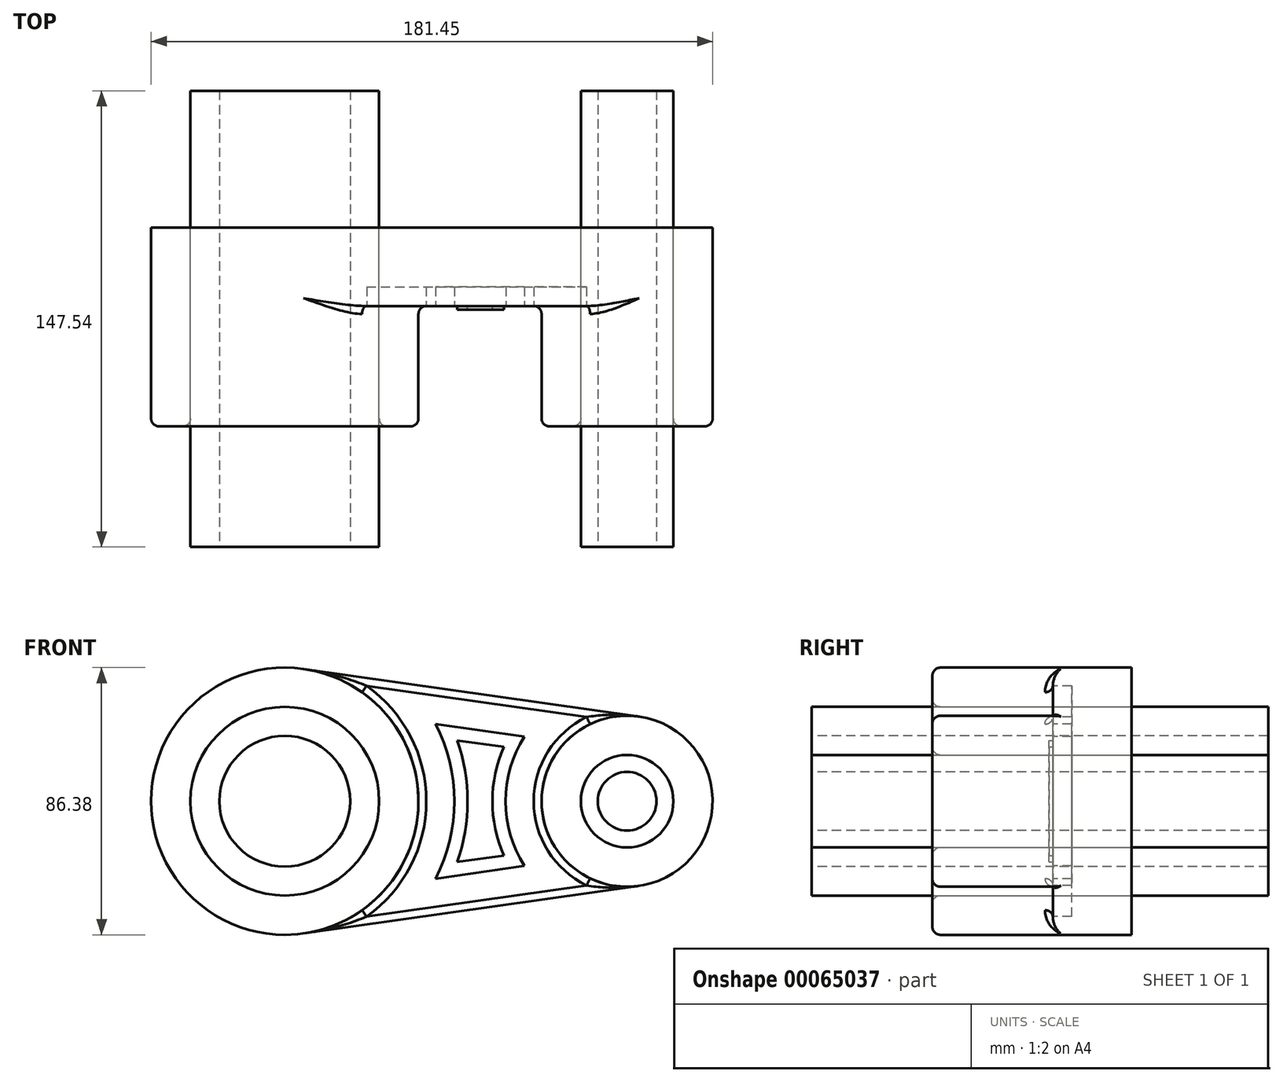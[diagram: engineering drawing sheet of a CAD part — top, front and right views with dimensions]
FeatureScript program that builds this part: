
annotation { "Feature Type Name" : "Feature", "Feature Type Description" : "" }
export const myFeature = defineFeature(function(context is Context, id is Id, definition is map)
    precondition{}
    {
        {
            var Q0;
            Q0=qCreatedBy(makeId("Front.planeOp"),FACE);
            var sketch = newSketch(context, id + "F0", { "sketchPlane" : qUnion([Q0])});
            skCircle(sketch, "E0", {"center": v(-144.17, 0) * mm, "radius": 43.2 * mm});
            skCircle(sketch, "E1", {"center": v(-33.55, 0) * mm, "radius": 27.65 * mm});
            skLineSegment(sketch, "E2", {"start": v(-138.1, -42.76) * mm, "end": v(-29.67, -27.37) * mm});
            skLineSegment(sketch, "E3", {"start": v(-138.1, 42.76) * mm, "end": v(-29.67, 27.37) * mm});
            skCircle(sketch, "E4.0", {"center": v(-144.17, 0) * mm, "radius": 30.5 * mm});
            skCircle(sketch, "E5.0", {"center": v(-33.55, 0) * mm, "radius": 14.95 * mm});
            skSolve(sketch);
        }
        {
            var Q0;
            Q0=makeQuery(id+"F0.imprint","IMPRINT",FACE,{"disambiguationData":[TD([[makeQuery(id+"F0.imprint","IMPRINT",EDGE,{"derivedFrom":sQuery(id+"F0.wireOp",EDGE,"E5.0")}),-1.0]])]});
            var Q1;
            {var subQ0=sQuery(id+"F0.wireOp",EDGE,"E2");Q1=makeQuery(id+"F0.imprint","IMPRINT",FACE,{"disambiguationData":[TD([[makeQuery(id+"F0.imprint","IMPRINT",EDGE,{"derivedFrom":subQ0}),1.0]])]});}
            var Q2;
            Q2=makeQuery(id+"F0.imprint","IMPRINT",FACE,{"disambiguationData":[TD([[makeQuery(id+"F0.imprint","IMPRINT",EDGE,{"derivedFrom":sQuery(id+"F0.wireOp",EDGE,"E4.0")}),-1.0]])]});
            extrude(context, id + "F1", {"entities" : qUnion([Q0, Q1, Q2]), "depth" : 25.4 * mm});
        }
        {
            var Q0;
            Q0=makeQuery(id+"F0.imprint","IMPRINT",FACE,{"disambiguationData":[TD([[makeQuery(id+"F0.imprint","IMPRINT",EDGE,{"derivedFrom":sQuery(id+"F0.wireOp",EDGE,"E4.0")}),-1.0]])]});
            var Q1;
            Q1=makeQuery(id+"F0.imprint","IMPRINT",FACE,{"disambiguationData":[TD([[makeQuery(id+"F0.imprint","IMPRINT",EDGE,{"derivedFrom":sQuery(id+"F0.wireOp",EDGE,"E5.0")}),-1.0]])]});
            extrude(context, id + "F2", {"entities" : qUnion([Q0, Q1]), "operationType" : NewBodyOperationType.ADD, "depth" : 64.3 * mm});
        }
        {
            var Q0;
            Q0=makeQuery(id+"F2.opExtrude","CAP_FACE",FACE,{"disambiguationData":[OSD([sQuery(id+"F0.wireOp",EDGE,"E0"),sQuery(id+"F0.wireOp",EDGE,"E4.0")])],"isStart":false});
            var Q1;
            Q1=makeQuery(id+"F2.opExtrude","CAP_FACE",FACE,{"disambiguationData":[OSD([sQuery(id+"F0.wireOp",EDGE,"E1"),sQuery(id+"F0.wireOp",EDGE,"E5.0")])],"isStart":false});
            var Q2;
            Q2=makeQuery(id+"F1.opExtrude","CAP_FACE",FACE,{"disambiguationData":[OSD([sQuery(id+"F0.wireOp",EDGE,"E0"),sQuery(id+"F0.wireOp",EDGE,"E1"),sQuery(id+"F0.wireOp",EDGE,"E2"),sQuery(id+"F0.wireOp",EDGE,"E3"),sQuery(id+"F0.wireOp",EDGE,"E4.0"),sQuery(id+"F0.wireOp",EDGE,"E5.0")])],"isStart":false});
            fillet(context, id + "F3", {"entities" : qUnion([Q0, Q1, Q2]), "radius" : 2.54 * mm, "tangentPropagation" : true, "allowEdgeOverflow" : false});
        }
        {
            var Q0;
            Q0=makeQuery(id+"F2.opExtrude","CAP_FACE",FACE,{"disambiguationData":[OSD([sQuery(id+"F0.wireOp",EDGE,"E0"),sQuery(id+"F0.wireOp",EDGE,"E4.0")])],"isStart":false});
            var sketch = newSketch(context, id + "F4", { "sketchPlane" : qUnion([Q0])});
            skCircle(sketch, "E6.0", {"center": v(-144.17, 0) * mm, "radius": 30.5 * mm});
            skCircle(sketch, "E6.1", {"center": v(-33.55, 0) * mm, "radius": 14.95 * mm});
            skSolve(sketch);
        }
        {
            var Q0;
            Q0 = qSketchRegion(id + "F4", true);
            extrude(context, id + "F5", {"entities" : qUnion([Q0]), "depth" : 147.53 * mm});
        }
        {
            var Q0;
            Q0=makeQuery(id+"F5.opExtrude","SWEPT_BODY",BODY,{"disambiguationData":[OSD([sQuery(id+"F4.wireOp",EDGE,"E6.0")])]});
            var Q1;
            Q1=makeQuery(id+"F5.opExtrude","SWEPT_BODY",BODY,{"disambiguationData":[OSD([sQuery(id+"F4.wireOp",EDGE,"E6.1")])]});
            transform(context, id + "F6", {"entities" : qUnion([Q0, Q1]), "transformType" : TransformType.TRANSLATION_3D, "dx" : 0 * mm, "dy" : 90.18 * mm, "dz" : 0 * mm, "makeCopy" : false});
        }
        {
            var Q0;
            Q0=makeQuery(id+"F5.opExtrude","CAP_FACE",FACE,{"disambiguationData":[OSD([sQuery(id+"F4.wireOp",EDGE,"E6.0")])],"isStart":false});
            var sketch = newSketch(context, id + "F7", { "sketchPlane" : qUnion([Q0])});
            skCircle(sketch, "E7.0", {"center": v(-33.55, 0) * mm, "radius": 9.47 * mm});
            skCircle(sketch, "E8.0", {"center": v(-144.17, 0) * mm, "radius": 21.14 * mm});
            skSolve(sketch);
        }
        {
            var Q0;
            Q0=makeQuery(id+"F7.imprint","IMPRINT",FACE,{"disambiguationData":[TD([[makeQuery(id+"F7.imprint","IMPRINT",EDGE,{"derivedFrom":sQuery(id+"F7.wireOp",EDGE,"E8.0")}),1.0]])]});
            var Q1;
            Q1=makeQuery(id+"F7.imprint","IMPRINT",FACE,{"disambiguationData":[TD([[makeQuery(id+"F7.imprint","IMPRINT",EDGE,{"derivedFrom":sQuery(id+"F7.wireOp",EDGE,"E7.0")}),1.0]])]});
            extrude(context, id + "F8", {"entities" : qUnion([Q0, Q1]), "operationType" : NewBodyOperationType.REMOVE, "oppositeDirection" : true, "depth" : 190.3 * mm});
        }
        {
            var Q0;
            Q0=makeQuery(id+"F5.opExtrude","SWEPT_BODY",BODY,{"disambiguationData":[OSD([sQuery(id+"F4.wireOp",EDGE,"E6.0")])]});
            var Q1;
            Q1=makeQuery(id+"F5.opExtrude","SWEPT_BODY",BODY,{"disambiguationData":[OSD([sQuery(id+"F4.wireOp",EDGE,"E6.1")])]});
            transform(context, id + "F9", {"entities" : qUnion([Q0, Q1]), "transformType" : TransformType.TRANSLATION_3D, "dx" : 0 * mm, "dy" : 61.42 * mm, "dz" : 0 * mm, "makeCopy" : false});
        }
        {
            var Q0;
            Q0=makeQuery(id+"F5.opExtrude","SWEPT_BODY",BODY,{"disambiguationData":[OSD([sQuery(id+"F4.wireOp",EDGE,"E6.0")])]});
            var Q1;
            Q1=makeQuery(id+"F5.opExtrude","SWEPT_BODY",BODY,{"disambiguationData":[OSD([sQuery(id+"F4.wireOp",EDGE,"E6.1")])]});
            transform(context, id + "F10", {"entities" : qUnion([Q0, Q1]), "transformType" : TransformType.TRANSLATION_3D, "dx" : 0 * mm, "dy" : -43.1 * mm, "dz" : 0 * mm, "makeCopy" : false});
        }
        {
            var Q0;
            Q0=makeQuery(id+"F1.opExtrude","CAP_FACE",FACE,{"disambiguationData":[OSD([sQuery(id+"F0.wireOp",EDGE,"E0"),sQuery(id+"F0.wireOp",EDGE,"E1"),sQuery(id+"F0.wireOp",EDGE,"E2"),sQuery(id+"F0.wireOp",EDGE,"E3"),sQuery(id+"F0.wireOp",EDGE,"E4.0"),sQuery(id+"F0.wireOp",EDGE,"E5.0")])],"isStart":false});
            var sketch = newSketch(context, id + "F11", { "sketchPlane" : qUnion([Q0])});
            skArc(sketch, "E9.0", {"start": v(-66.72, -20.94) * mm, "mid": v(-72.78, 0) * mm, "end": v(-66.72, 20.94) * mm});
            skLineSegment(sketch, "E9.1", {"start": v(-95.45, -25.02) * mm, "end": v(-66.72, -20.94) * mm});
            skArc(sketch, "E9.2", {"start": v(-95.45, 25.02) * mm, "mid": v(-89.4, 0) * mm, "end": v(-95.45, -25.02) * mm});
            skLineSegment(sketch, "E9.3", {"start": v(-66.72, 20.94) * mm, "end": v(-95.45, 25.02) * mm});
            skSolve(sketch);
        }
        {
            var Q0;
            Q0=makeQuery(id+"F11.imprint","IMPRINT",FACE,{"disambiguationData":[TD([[makeQuery(id+"F11.imprint","IMPRINT",EDGE,{"derivedFrom":sQuery(id+"F11.wireOp",EDGE,"E9.0")}),1.0]])]});
            extrude(context, id + "F12", {"entities" : qUnion([Q0]), "operationType" : NewBodyOperationType.REMOVE, "oppositeDirection" : true, "depth" : 6.16 * mm});
        }
        {
            var Q0;
            Q0=makeQuery(id+"F12.boolean.opBoolean","COPY",FACE,{"derivedFrom":makeQuery(id+"F12.opExtrude","CAP_FACE",FACE,{"disambiguationData":[OSD([sQuery(id+"F11.wireOp",EDGE,"E9.0"),sQuery(id+"F11.wireOp",EDGE,"E9.1"),sQuery(id+"F11.wireOp",EDGE,"E9.2"),sQuery(id+"F11.wireOp",EDGE,"E9.3")])],"isStart":false})});
            var sketch = newSketch(context, id + "F13", { "sketchPlane" : qUnion([Q0])});
            skLineSegment(sketch, "E10.0", {"start": v(-88.47, -19.68) * mm, "end": v(-73.4, -17.54) * mm});
            skArc(sketch, "E10.1", {"start": v(-88.47, 19.68) * mm, "mid": v(-85.1, 0) * mm, "end": v(-88.47, -19.68) * mm});
            skLineSegment(sketch, "E10.2", {"start": v(-73.4, 17.54) * mm, "end": v(-88.47, 19.68) * mm});
            skArc(sketch, "E10.3", {"start": v(-73.4, -17.54) * mm, "mid": v(-77.08, 0) * mm, "end": v(-73.4, 17.54) * mm});
            skSolve(sketch);
        }
        {
            var Q0;
            Q0=makeQuery(id+"F13.imprint","IMPRINT",FACE,{"disambiguationData":[TD([[makeQuery(id+"F13.imprint","IMPRINT",EDGE,{"derivedFrom":sQuery(id+"F13.wireOp",EDGE,"E10.0")}),1.0]])]});
            extrude(context, id + "F14", {"entities" : qUnion([Q0]), "operationType" : NewBodyOperationType.ADD, "depth" : 7.38 * mm});
        }
    });
